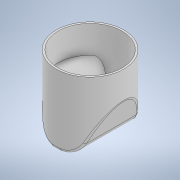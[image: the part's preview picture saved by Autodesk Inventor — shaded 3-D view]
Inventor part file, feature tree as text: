
AUTODESK INVENTOR PART (.ipt)
format: ipt  version: 2020 (Build 240168000, 168)  size: 279,040 bytes
history: native  units: in
note: dims shown in document units (in); Inventor stores cm internally (conversion verified against a paired STEP export)
features: extrude x5, sketch x5, fillet x3
ambient origin geometry x8: Origin, YZ Plane, XZ Plane, XY Plane, X Axis, Y Axis, Z Axis, Center Point
bodies: Solid1 (feature_tree)
feature tree (13):
  extrude  "Extrusion1"  Depth=1.063in
  extrude  "Extrusion2"  Depth=1.0039in
  extrude  "Extrusion3"  Depth=0.2165in
  extrude  "Extrusion4"  Depth=0.6102in TaperAngle=0.0deg
  extrude  "Extrusion5"  Depth=0.0394in
  fillet  "Fillet1"  Radius=1.1024in
  fillet  "Fillet2"  Radius=1.1024in
  fillet  "Fillet3"  Radius=0.3in
  sketch  "Sketch1"  dims[d0=1.063in d1=1.063in]
  sketch  "Sketch2"  dims[d2=1.1024in d3=0.0in d4=1.0039in]
  sketch  "Sketch3"  dims[d5=0.4331in d6=0.0in d7=0.2165in]
  sketch  "Sketch4"  dims[d8=0.2165in d9=0.6102in d10=0.0in]
  sketch  "Sketch5"  dims[d11=0.0394in d12=0.0394in d13=1.1024in d14=0.0in d15=1.1024in d16=0.0in d17=0.3in d18=0.3in d19=0.05in]
